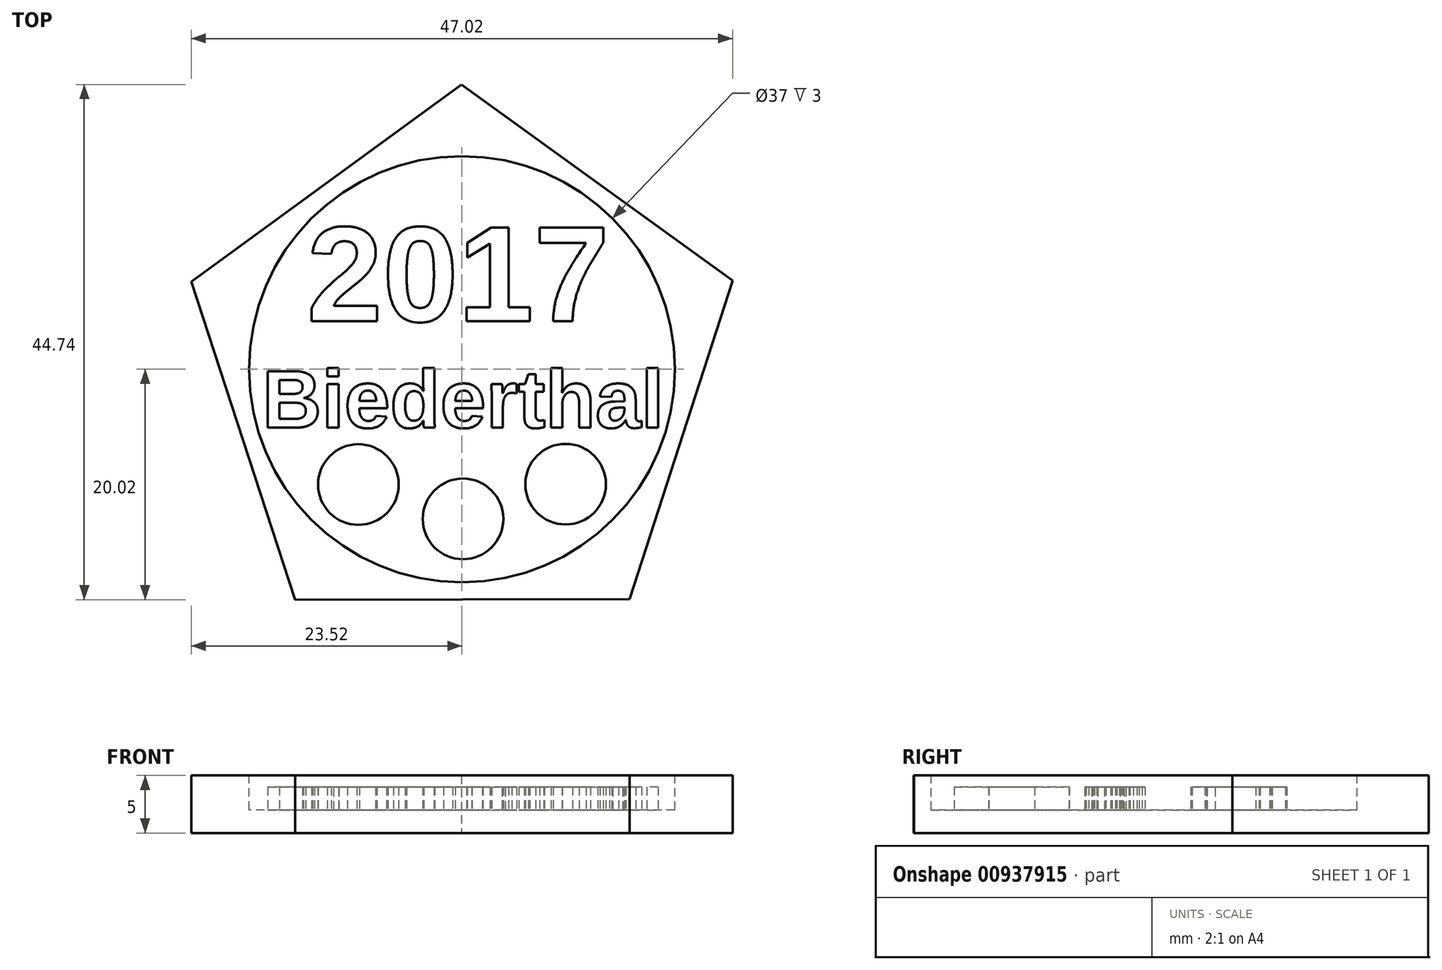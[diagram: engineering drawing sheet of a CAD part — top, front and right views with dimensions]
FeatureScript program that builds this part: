
annotation { "Feature Type Name" : "Feature", "Feature Type Description" : "" }
export const myFeature = defineFeature(function(context is Context, id is Id, definition is map)
    precondition{}
    {
        {
            var Q0;
            Q0=qCreatedBy(makeId("Top.planeOp"),FACE);
            var sketch = newSketch(context, id + "F0", { "sketchPlane" : qUnion([Q0])});
            skCircle(sketch, "E0.cCircle", {"center": v(0, 0) * mm, "radius": 20 * mm, "construction": true});
            skLineSegment(sketch, "E0.0", {"start": v(-23.52, 7.6) * mm, "end": v(-0.04, 24.72) * mm});
            skLineSegment(sketch, "E0.1", {"start": v(-0.04, 24.72) * mm, "end": v(23.5, 7.68) * mm});
            skLineSegment(sketch, "E0.2", {"start": v(23.5, 7.68) * mm, "end": v(14.56, -19.98) * mm});
            skLineSegment(sketch, "E0.3", {"start": v(14.56, -19.98) * mm, "end": v(-14.5, -20.02) * mm});
            skLineSegment(sketch, "E0.4", {"start": v(-14.5, -20.02) * mm, "end": v(-23.52, 7.6) * mm});
            skPoint(sketch, "E0.0.midPoint", {"position": v(-11.78, 16.16) * mm});
            skSolve(sketch);
        }
        {
            var Q0;
            Q0 = qSketchRegion(id + "F0", true);
            extrude(context, id + "F1", {"entities" : qUnion([Q0]), "depth" : 5 * mm, "offsetDistance" : 25 * mm});
        }
        {
            var Q0;
            Q0=makeQuery(id+"F1.opExtrude","CAP_FACE",FACE,{"disambiguationData":[OSD([sQuery(id+"F0.wireOp",EDGE,"E0.0"),sQuery(id+"F0.wireOp",EDGE,"E0.1"),sQuery(id+"F0.wireOp",EDGE,"E0.2"),sQuery(id+"F0.wireOp",EDGE,"E0.3"),sQuery(id+"F0.wireOp",EDGE,"E0.4")])],"isStart":false});
            var sketch = newSketch(context, id + "F2", { "sketchPlane" : qUnion([Q0])});
            skCircle(sketch, "E1", {"center": v(0, 0) * mm, "radius": 18.5 * mm});
            skSolve(sketch);
        }
        {
            var Q0;
            {var subQ0=sQuery(id+"F2.wireOp",EDGE,"E1");var subQ4=makeQuery(id+"F2.imprint","INTERSECT",VERTEX,{"derivedFrom":[makeQuery(id+"F1.opExtrude","CAP_EDGE",EDGE,{"disambiguationData":[OSD([sQuery(id+"F0.wireOp",EDGE,"E0.0")])],"isStart":false}),subQ0]});Q0=makeQuery(id+"F2.imprint","IMPRINT",FACE,{"disambiguationData":[TD([[makeQuery(id+"F2.imprint","IMPRINT",EDGE,{"disambiguationData":[TD([[subQ4,1.0]])],"derivedFrom":subQ0}),1.0]])]});}
            extrude(context, id + "F3", {"entities" : qUnion([Q0]), "operationType" : NewBodyOperationType.REMOVE, "oppositeDirection" : true, "depth" : 3 * mm, "offsetDistance" : 25 * mm});
        }
        {
            var Q0;
            Q0=makeQuery(id+"F3.boolean.opBoolean","COPY",FACE,{"derivedFrom":makeQuery(id+"F3.opExtrude","CAP_FACE",FACE,{"disambiguationData":[OSD([sQuery(id+"F2.wireOp",EDGE,"E1")])],"isStart":false})});
            var sketch = newSketch(context, id + "F4", { "sketchPlane" : qUnion([Q0])});
            skText(sketch, "E2", { "text": "2017", "fontName": "Arimo-Bold.ttf"});
            skText(sketch, "E3", { "text": "Biederthal", "fontName": "Arimo-Bold.ttf"});
            skCircle(sketch, "E4", {"center": v(0.1, -13) * mm, "radius": 3.5 * mm});
            skCircle(sketch, "E5", {"center": v(-9, -10.01) * mm, "radius": 3.5 * mm});
            skCircle(sketch, "E6", {"center": v(9, -9.99) * mm, "radius": 3.5 * mm});
            const initialGuessF4  = {"E2": [-0.01346, 0.00416, 1, 0, 0.0085], "E3": [-0.01736, -0.00508, 1, 0, 0.00514]};
            skSetInitialGuess(sketch, initialGuessF4);
            skSolve(sketch);
        }
        {
            var Q0;
            Q0 = qSketchRegion(id + "F4", true);
            extrude(context, id + "F5", {"entities" : qUnion([Q0]), "operationType" : NewBodyOperationType.ADD, "depth" : 2 * mm, "offsetDistance" : 25 * mm});
        }
    });
